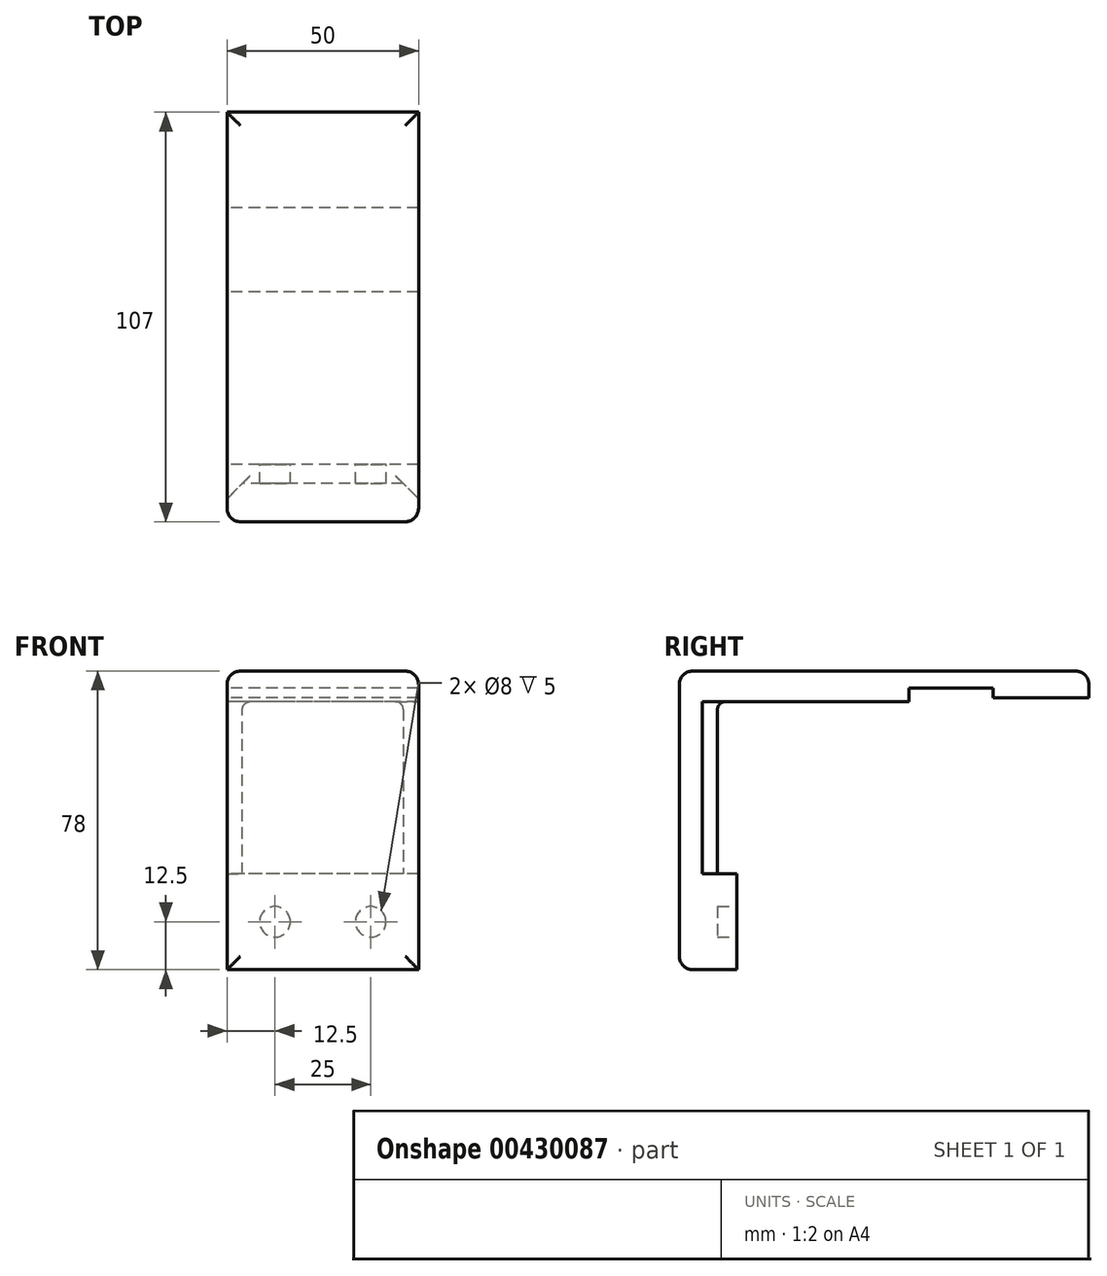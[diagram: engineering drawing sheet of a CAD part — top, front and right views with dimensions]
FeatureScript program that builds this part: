
annotation { "Feature Type Name" : "Feature", "Feature Type Description" : "" }
export const myFeature = defineFeature(function(context is Context, id is Id, definition is map)
    precondition{}
    {
        {
            var Q0;
            Q0=qCreatedBy(makeId("Right.planeOp"),FACE);
            var sketch = newSketch(context, id + "F0", { "sketchPlane" : qUnion([Q0])});
            skLineSegment(sketch, "E0", {"start": v(-10, 8) * mm, "end": v(97, 8) * mm});
            skLineSegment(sketch, "E1", {"start": v(97, 8) * mm, "end": v(97, 1) * mm});
            skLineSegment(sketch, "E2", {"start": v(97, 1) * mm, "end": v(72, 1) * mm});
            skLineSegment(sketch, "E3", {"start": v(72, 1) * mm, "end": v(72, 3.5) * mm});
            skLineSegment(sketch, "E4", {"start": v(72, 3.5) * mm, "end": v(50, 3.5) * mm});
            skLineSegment(sketch, "E5", {"start": v(50, 3.5) * mm, "end": v(50, 0) * mm});
            skLineSegment(sketch, "E6", {"start": v(50, 0) * mm, "end": v(0, 0) * mm});
            skLineSegment(sketch, "E7", {"start": v(0, 0) * mm, "end": v(0, -45) * mm});
            skLineSegment(sketch, "E8", {"start": v(0, -45) * mm, "end": v(5, -45) * mm});
            skLineSegment(sketch, "E9", {"start": v(5, -45) * mm, "end": v(5, -70) * mm});
            skLineSegment(sketch, "E10", {"start": v(5, -70) * mm, "end": v(-10, -70) * mm});
            skLineSegment(sketch, "E11", {"start": v(-10, -70) * mm, "end": v(-10, 8) * mm});
            skSolve(sketch);
        }
        {
            var Q0;
            Q0=makeQuery(id+"F0.imprint","IMPRINT",FACE,{"disambiguationData":[TD([[makeQuery(id+"F0.imprint","IMPRINT",EDGE,{"derivedFrom":sQuery(id+"F0.wireOp",EDGE,"E0")}),-1.0]])]});
            extrude(context, id + "F1", {"entities" : qUnion([Q0]), "depth" : 50 * mm});
        }
        {
            var Q0;
            Q0=makeQuery(id+"F1.opExtrude","SWEPT_EDGE",EDGE,{"disambiguationData":[OSD([sQuery(id+"F0.wireOp",EDGE,"E0"),sQuery(id+"F0.wireOp",EDGE,"E11")])]});
            fillet(context, id + "F2", {"entities" : qUnion([Q0]), "radius" : 3.5 * mm, "tangentPropagation" : true, "allowEdgeOverflow" : false});
        }
        {
            var Q0;
            Q0=makeQuery(id+"F1.opExtrude","CAP_EDGE",EDGE,{"disambiguationData":[OSD([sQuery(id+"F0.wireOp",EDGE,"E0")])],"isStart":false});
            var Q1;
            Q1=makeQuery(id+"F1.opExtrude","SWEPT_EDGE",EDGE,{"disambiguationData":[OSD([sQuery(id+"F0.wireOp",EDGE,"E0"),sQuery(id+"F0.wireOp",EDGE,"E1")])]});
            var Q2;
            Q2=makeQuery(id+"F1.opExtrude","CAP_EDGE",EDGE,{"disambiguationData":[OSD([sQuery(id+"F0.wireOp",EDGE,"E0")])],"isStart":true});
            var Q3;
            Q3=makeQuery(id+"F1.opExtrude","SWEPT_EDGE",EDGE,{"disambiguationData":[OSD([sQuery(id+"F0.wireOp",EDGE,"E10"),sQuery(id+"F0.wireOp",EDGE,"E11")])]});
            fillet(context, id + "F3", {"entities" : qUnion([Q0, Q1, Q2, Q3]), "radius" : 3.5 * mm, "tangentPropagation" : true, "allowEdgeOverflow" : false});
        }
        {
            var Q0;
            Q0=makeQuery(id+"F1.opExtrude","SWEPT_FACE",FACE,{"disambiguationData":[OSD([sQuery(id+"F0.wireOp",EDGE,"E9")])]});
            var sketch = newSketch(context, id + "F4", { "sketchPlane" : qUnion([Q0])});
            skCircle(sketch, "E12", {"center": v(-37.5, -57.5) * mm, "radius": 4 * mm});
            skCircle(sketch, "E13", {"center": v(-12.5, -57.5) * mm, "radius": 4 * mm});
            skSolve(sketch);
        }
        {
            var Q0;
            Q0=makeQuery(id+"F4.imprint","IMPRINT",FACE,{"disambiguationData":[TD([[makeQuery(id+"F4.imprint","IMPRINT",EDGE,{"derivedFrom":sQuery(id+"F4.wireOp",EDGE,"E12")}),1.0]])]});
            var Q1;
            Q1=makeQuery(id+"F4.imprint","IMPRINT",FACE,{"disambiguationData":[TD([[makeQuery(id+"F4.imprint","IMPRINT",EDGE,{"derivedFrom":sQuery(id+"F4.wireOp",EDGE,"E13")}),1.0]])]});
            extrude(context, id + "F5", {"entities" : qUnion([Q0, Q1]), "operationType" : NewBodyOperationType.REMOVE, "oppositeDirection" : true, "depth" : 5 * mm});
        }
        {
            var Q0;
            Q0=makeQuery(id+"F1.opExtrude","CAP_EDGE",EDGE,{"disambiguationData":[OSD([sQuery(id+"F0.wireOp",EDGE,"E7")])],"isStart":false});
            var Q1;
            Q1=makeQuery(id+"F1.opExtrude","CAP_EDGE",EDGE,{"disambiguationData":[OSD([sQuery(id+"F0.wireOp",EDGE,"E7")])],"isStart":true});
            chamfer(context, id + "F6", {"entities" : qUnion([Q0, Q1]), "width" : 4 * mm, "tangentPropagation" : true});
        }
        {
            var Q0;
            Q0=makeQuery(id+"F1.opExtrude","SWEPT_EDGE",EDGE,{"disambiguationData":[OSD([sQuery(id+"F0.wireOp",EDGE,"E6"),sQuery(id+"F0.wireOp",EDGE,"E7")])]});
            fillet(context, id + "F7", {"entities" : qUnion([Q0]), "radius" : 2 * mm, "tangentPropagation" : true, "allowEdgeOverflow" : false});
        }
    });
